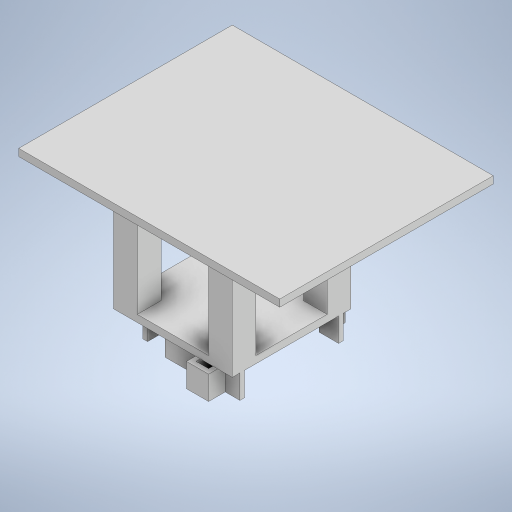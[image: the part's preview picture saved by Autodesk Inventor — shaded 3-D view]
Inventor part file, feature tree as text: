
AUTODESK INVENTOR PART (.ipt)
format: ipt  version: 2024 (Build 280153020, 153B)  size: 331,776 bytes
history: native  units: in
note: dims shown in document units (in); Inventor stores cm internally (conversion verified against a paired STEP export)
features: extrude x4, sketch x3
ambient origin geometry x8: Origin, YZ Plane, XZ Plane, XY Plane, X Axis, Y Axis, Z Axis, Center Point
bodies: Solid1 (feature_tree)
feature tree (7):
  sketch  "Sketch1"  dims[d0=0.3937in d1=0.3937in]
  extrude  "Extrusion1"  Depth=0.3937in
  extrude  "Extrusion2"  TaperAngle=0.0deg  [1 undecoded]
  extrude  "Extrusion3"  TaperAngle=0.0deg  [1 undecoded]
  extrude  "Extrusion4"  Depth=0.7874in
  sketch  "Sketch2"  dims[d2=0.0in d3=0.0in]
  sketch  "Sketch3"  dims[d4=0.0in d5=0.0in d6=0.7874in d8=1.5748in d9=0.7874in d11=1.5748in d14=1.9685in d15=1.9685in d16=0.1181in d17=0.0in d18=2.1887in d19=0.0in d20=1.5591in d22=1.61in d23=0.322in d25=0.2089in d26=0.2756in d30=0.0787in d31=0.0787in d32=0.0787in d33=0.0787in d36=0.0787in d37=0.0787in d38=0.0787in d40=0.3937in d41=0.0in d42=0.7874in d43=0.7874in d44=0.7874in d45=0.7874in d46=0.7874in d47=1.5748in d48=0.7874in d49=0.7874in d50=0.1181in d51=0.0in d53=0.0in d54=0.6299in d55=0.0787in d56=0.0787in]
note: 2 required parameter values undecoded (feature->parameter linkage not recoverable at this tier; creation-order binding heuristic only, values carry confidence <= 0.55)
